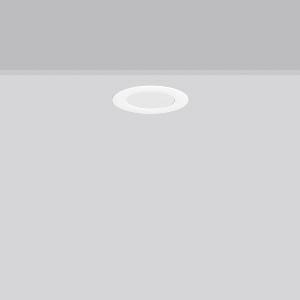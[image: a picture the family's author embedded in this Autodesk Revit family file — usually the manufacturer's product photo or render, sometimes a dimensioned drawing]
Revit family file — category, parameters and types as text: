
# Revit family: toledo_flat_round_e_901451_002_76_67b3
name_source: partatom
category: Lighting Fixtures
units: mm (PartAtom-declared; Revit-internal decimal feet)

## family parameters
Cut with Voids When Loaded = No
Host = Face
Light Source = No
Part Type = Normal
Room Calculation Point = No
Round Connector Dimension = Use Diameter
Shared = No

## types (1)
- TOLEDO FLAT round E (1 x LED Modul 830, 470 lm, 3000)
    Apparent Load = 5 VA
    CIE Flux Codes = 48 79 96 100 100
    Color Rendering = 80
    Color Temperature = 3000
    Default Elevation = 1800 mm
    Description = Series: TOLEDO FLAT round
Ultra thin recessed downlight. Housing: die-cast aluminium. Light guide and diffuser made of non-yellowing PMMA, opal matt. Ceiling installation with spring system. Mounting depth depends on ceiling strength. Including separate LED converter with connecting cable 250 mm. Suitable for through-wiring with separately available accessories. Surface mounted housing as accessory for all sizes. Retrofittable decorative cylinders made of chintz fabric as accessory, optional with satin finish plastic diffuser. Through-wiring box (5 pole) available as accessory. 
Colour: white
Diameter: 148 mm
Height: 2 mm
Cut-out diameter: 128 mm
Recess height: 31-53 mm
Luminaire: recess height: 31-51 mm
Lamp: LED
Socket: without socket
Colour temperature: 3000K
Colour rendering index (CRI): 80
System power: 5 W
Rated luminous flux: 470 lm
Luminous efficiency: 94 lm/W
Control gear: Converter, dimmable, DALI
Protection class: II
Type of protection: IP 54
    Height = 0 mm  [stored 0 ft]
    Lamp = 1 x LED Modul 830
    Lamp Light Flux = 470 lm
    Lamp count = 1
    Length = 148 mm
    Lifetime = 50000 h
    Luminous efficacy = 94 lm/W
    Manufacturer = RZB
    ModVariant = No
    Model = 901451.002.76
    Mounting Place = Ceiling
    Mounting Type = Recessed
    Number of Poles = 1
    OnlyDefault = Yes
    Power Factor = 1
    Product Name = TOLEDO FLAT round E
    Product group = Recessed downlights
    ProductGroupID = 402
    Protection Class = Protection class II
    Protection Degree = IP 20
    RLX_Detail_Level = 1
    RLX_Emergency_Light_Flux = 0 lm
    RLX_Emergency_Type = 0
    RLX_Emergency_Type_DB = No
    RlxData = <blob elided: 75181 chars, md5=0098dc7e>
    Socket = socket
    Standby Power = 0 W
    System Light Flux = 470 lm
    System Power = 5 W
    Type Comments = Product without accessories
    Type Image = 901451.002.jpg
    URL = http://relux.com
    VarID = ---
    Voltage = 230 V
    Voltage Range = 220-240 V
    Weight = 0.00 kg
    Width = 0 mm  [stored 0 ft]

note: [stored X ft] marks values corroborated as IEEE doubles in the binary element streams (Revit-internal decimal feet)

## geometry (parser evidence)
native form markers: Blend x4, Sweep x8
no freeform markers — native parametric forms only
